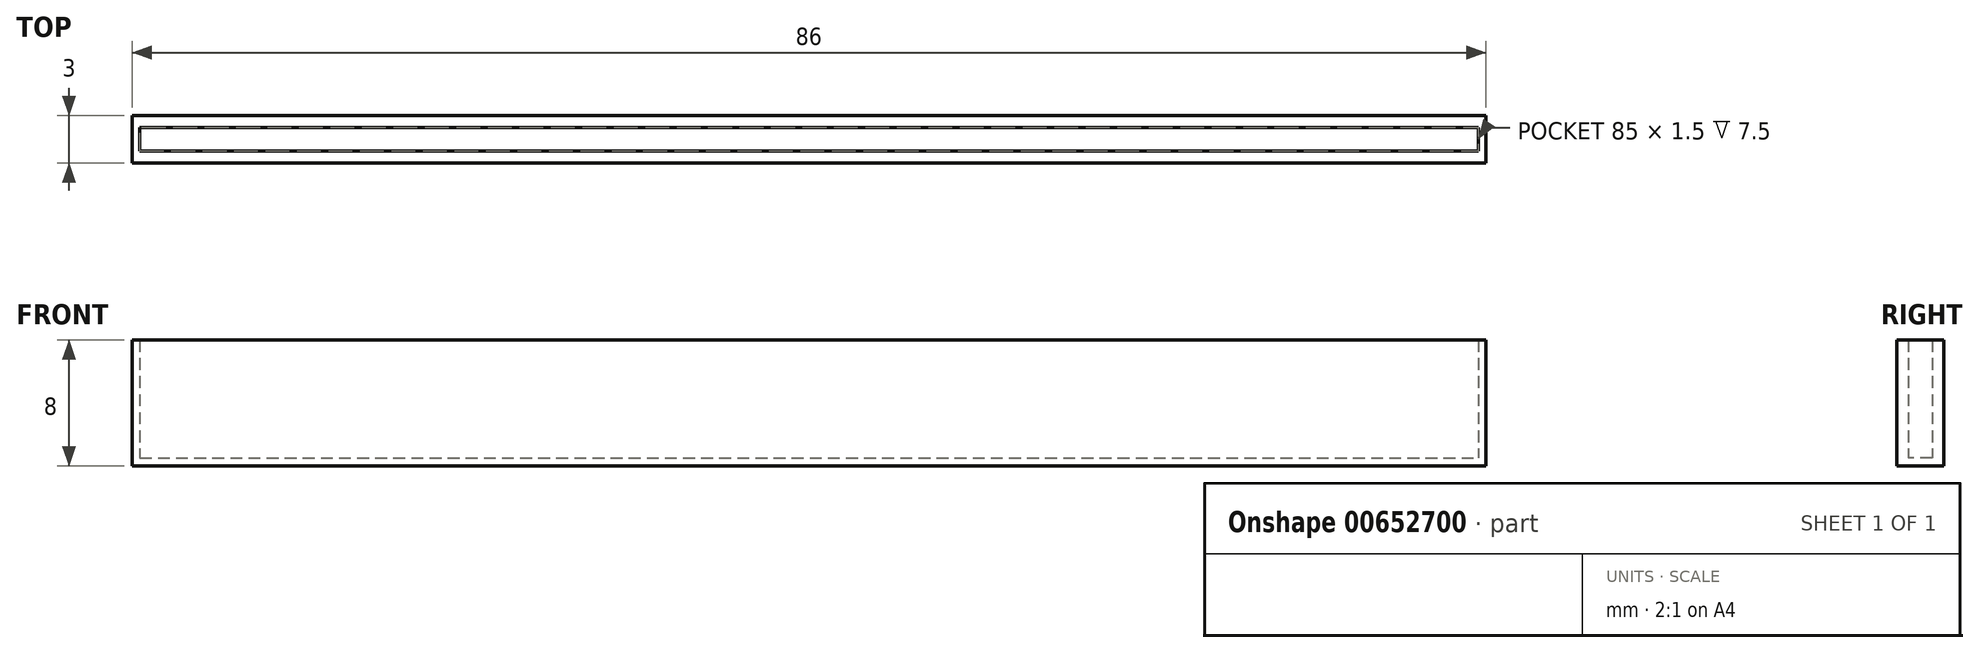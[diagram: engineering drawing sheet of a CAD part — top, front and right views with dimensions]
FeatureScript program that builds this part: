
annotation { "Feature Type Name" : "Feature", "Feature Type Description" : "" }
export const myFeature = defineFeature(function(context is Context, id is Id, definition is map)
    precondition{}
    {
        {
            var Q0;
            Q0=qCreatedBy(makeId("Top.planeOp"),FACE);
            var sketch = newSketch(context, id + "F0", { "sketchPlane" : qUnion([Q0])});
            skLineSegment(sketch, "E0.bottom", {"start": v(-43, 1.5) * mm, "end": v(43, 1.5) * mm});
            skLineSegment(sketch, "E0.top", {"start": v(-43, -1.5) * mm, "end": v(43, -1.5) * mm});
            skLineSegment(sketch, "E0.left", {"start": v(-43, 1.5) * mm, "end": v(-43, -1.5) * mm});
            skLineSegment(sketch, "E0.right", {"start": v(43, 1.5) * mm, "end": v(43, -1.5) * mm});
            skLineSegment(sketch, "E1", {"start": v(0, 1.5) * mm, "end": v(0, -1.5) * mm, "construction": true});
            skLineSegment(sketch, "E2", {"start": v(43, 0) * mm, "end": v(-43, 0) * mm, "construction": true});
            skPoint(sketch, "E3", {"position": v(0, 0) * mm});
            skLineSegment(sketch, "E4.bottom", {"start": v(-42.5, 0.75) * mm, "end": v(42.5, 0.75) * mm});
            skLineSegment(sketch, "E4.top", {"start": v(-42.5, -0.75) * mm, "end": v(42.5, -0.75) * mm});
            skLineSegment(sketch, "E4.left", {"start": v(-42.5, 0.75) * mm, "end": v(-42.5, -0.75) * mm});
            skLineSegment(sketch, "E4.right", {"start": v(42.5, 0.75) * mm, "end": v(42.5, -0.75) * mm});
            skPoint(sketch, "E5", {"position": v(42.5, 0) * mm});
            skPoint(sketch, "E6", {"position": v(0, 0.75) * mm});
            skSolve(sketch);
        }
        {
            var Q0;
            Q0=makeQuery(id+"F0.imprint","IMPRINT",FACE,{"disambiguationData":[TD([[makeQuery(id+"F0.imprint","IMPRINT",EDGE,{"derivedFrom":sQuery(id+"F0.wireOp",EDGE,"E4.bottom")}),-1.0]])]});
            extrude(context, id + "F1", {"entities" : qUnion([Q0]), "depth" : .5 * mm, "offsetDistance" : 25 * mm});
        }
        {
            var Q0;
            Q0=makeQuery(id+"F0.imprint","IMPRINT",FACE,{"disambiguationData":[TD([[makeQuery(id+"F0.imprint","IMPRINT",EDGE,{"derivedFrom":sQuery(id+"F0.wireOp",EDGE,"E0.bottom")}),-1.0]])]});
            extrude(context, id + "F2", {"entities" : qUnion([Q0]), "operationType" : NewBodyOperationType.ADD, "depth" : 8 * mm, "offsetDistance" : 25 * mm});
        }
    });
